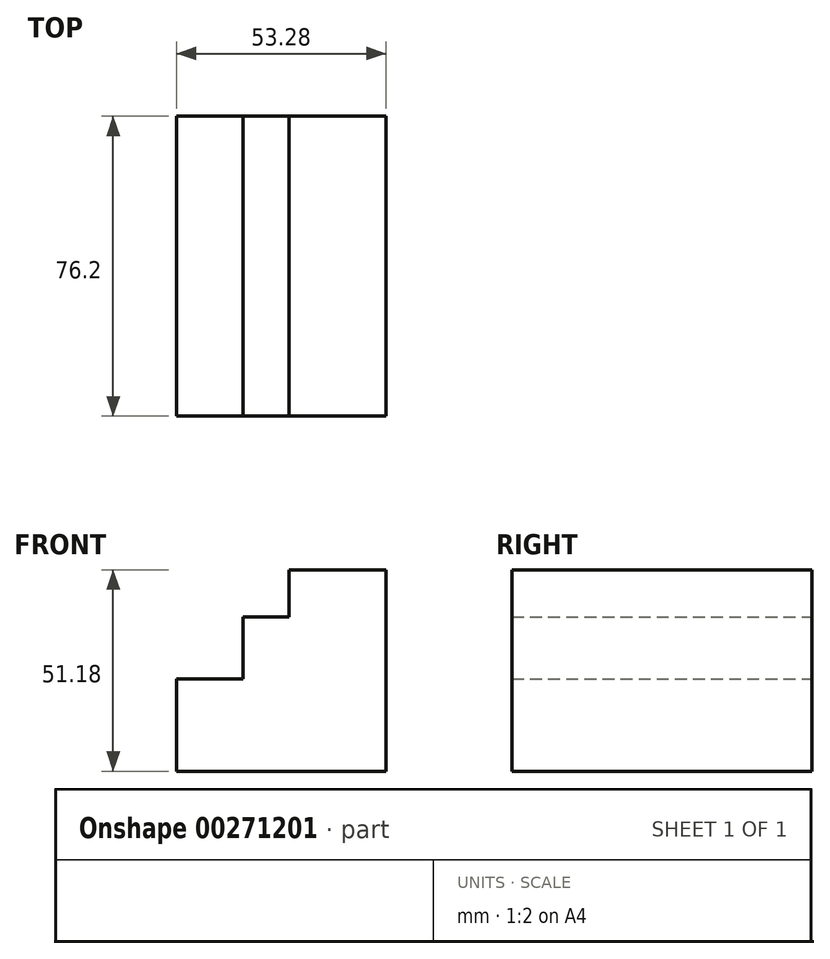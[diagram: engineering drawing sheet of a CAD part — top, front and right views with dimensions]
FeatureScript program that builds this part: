
annotation { "Feature Type Name" : "Feature", "Feature Type Description" : "" }
export const myFeature = defineFeature(function(context is Context, id is Id, definition is map)
    precondition{}
    {
        {
            var Q0;
            Q0=qCreatedBy(makeId("Front.planeOp"),FACE);
            var sketch = newSketch(context, id + "F0", { "sketchPlane" : qUnion([Q0])});
            skLineSegment(sketch, "E0.bottom", {"start": v(0, 0) * mm, "end": v(-53.28, 0) * mm});
            skLineSegment(sketch, "E0.top", {"start": v(0, 23.49) * mm, "end": v(-53.28, 23.49) * mm});
            skLineSegment(sketch, "E0.left", {"start": v(0, 0) * mm, "end": v(0, 23.49) * mm});
            skLineSegment(sketch, "E0.right", {"start": v(-53.28, 0) * mm, "end": v(-53.28, 23.49) * mm});
            skLineSegment(sketch, "E1.bottom", {"start": v(-36.28, 23.49) * mm, "end": v(0, 23.49) * mm});
            skLineSegment(sketch, "E1.top", {"start": v(-36.28, 39.15) * mm, "end": v(0, 39.15) * mm});
            skLineSegment(sketch, "E1.left", {"start": v(-36.28, 23.49) * mm, "end": v(-36.28, 39.15) * mm});
            skLineSegment(sketch, "E1.right", {"start": v(0, 23.49) * mm, "end": v(0, 39.15) * mm});
            skLineSegment(sketch, "E2.bottom", {"start": v(-24.63, 39.15) * mm, "end": v(0, 39.15) * mm});
            skLineSegment(sketch, "E2.top", {"start": v(-24.63, 51.18) * mm, "end": v(0, 51.18) * mm});
            skLineSegment(sketch, "E2.left", {"start": v(-24.63, 39.15) * mm, "end": v(-24.63, 51.18) * mm});
            skLineSegment(sketch, "E2.right", {"start": v(0, 39.15) * mm, "end": v(0, 51.18) * mm});
            skSolve(sketch);
        }
        {
            var Q0;
            Q0 = qSketchRegion(id + "F0", true);
            extrude(context, id + "F1", {"entities" : qUnion([Q0]), "depth" : 76.2 * mm});
        }
    });
